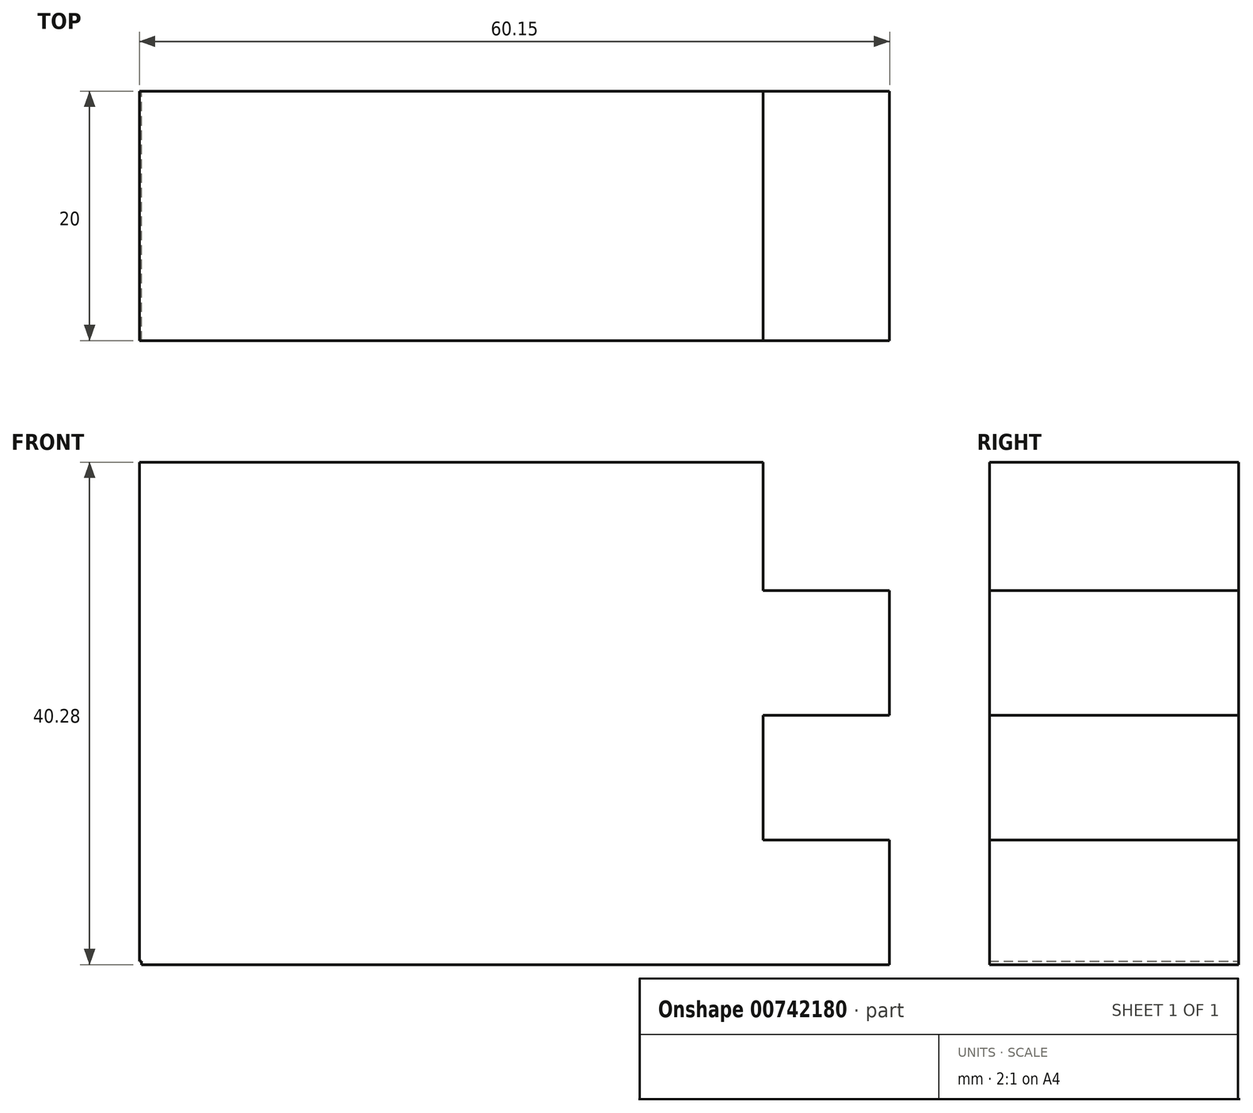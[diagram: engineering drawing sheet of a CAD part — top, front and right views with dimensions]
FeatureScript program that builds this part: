
annotation { "Feature Type Name" : "Feature", "Feature Type Description" : "" }
export const myFeature = defineFeature(function(context is Context, id is Id, definition is map)
    precondition{}
    {
        {
            var Q0;
            Q0=qCreatedBy(makeId("Front.planeOp"),FACE);
            var sketch = newSketch(context, id + "F0", { "sketchPlane" : qUnion([Q0])});
            skLineSegment(sketch, "E0.bottom", {"start": v(-3.97, 22.58) * mm, "end": v(46.03, 22.58) * mm});
            skLineSegment(sketch, "E0.top", {"start": v(-3.97, -17.42) * mm, "end": v(46.03, -17.42) * mm});
            skLineSegment(sketch, "E0.left", {"start": v(-3.97, 22.58) * mm, "end": v(-3.97, -17.42) * mm});
            skLineSegment(sketch, "E0.right", {"start": v(46.03, 22.58) * mm, "end": v(46.03, -17.42) * mm});
            skSolve(sketch);
        }
        {
            var Q0;
            Q0=qCreatedBy(makeId("Front.planeOp"),FACE);
            var sketch = newSketch(context, id + "F1", { "sketchPlane" : qUnion([Q0])});
            skLineSegment(sketch, "E1.bottom", {"start": v(-3.82, -7.7) * mm, "end": v(56.18, -7.7) * mm});
            skLineSegment(sketch, "E1.top", {"start": v(-3.82, -17.7) * mm, "end": v(56.18, -17.7) * mm});
            skLineSegment(sketch, "E1.left", {"start": v(-3.82, -7.7) * mm, "end": v(-3.82, -17.7) * mm});
            skLineSegment(sketch, "E1.right", {"start": v(56.18, -7.7) * mm, "end": v(56.18, -17.7) * mm});
            skLineSegment(sketch, "E2", {"start": v(36.18, -7.7) * mm, "end": v(36.18, 12.3) * mm});
            skLineSegment(sketch, "E3", {"start": v(56.18, -7.7) * mm, "end": v(56.18, 12.3) * mm});
            skLineSegment(sketch, "E4", {"start": v(36.18, 12.3) * mm, "end": v(56.18, 12.3) * mm});
            skLineSegment(sketch, "E5.top", {"start": v(36.18, 2.3) * mm, "end": v(56.18, 2.3) * mm});
            skLineSegment(sketch, "E5.left", {"start": v(36.18, 12.3) * mm, "end": v(36.18, 2.3) * mm});
            skLineSegment(sketch, "E5.right", {"start": v(56.18, 12.3) * mm, "end": v(56.18, 2.3) * mm});
            skSolve(sketch);
        }
        {
            var Q0;
            Q0 = qSketchRegion(id + "F0", true);
            extrude(context, id + "F2", {"entities" : qUnion([Q0]), "depth" : 20 * mm, "offsetDistance" : 25 * mm});
        }
        {
            var Q0;
            Q0=makeQuery(id+"F1.imprint","IMPRINT",FACE,{"disambiguationData":[TD([[makeQuery(id+"F1.imprint","IMPRINT",EDGE,{"derivedFrom":sQuery(id+"F1.wireOp",EDGE,"E4")}),-1.0]])]});
            extrude(context, id + "F3", {"entities" : qUnion([Q0]), "operationType" : NewBodyOperationType.ADD, "depth" : 20 * mm, "offsetDistance" : 25 * mm});
        }
        {
            var Q0;
            Q0=makeQuery(id+"F1.imprint","IMPRINT",FACE,{"disambiguationData":[TD([[makeQuery(id+"F1.imprint","IMPRINT",EDGE,{"derivedFrom":sQuery(id+"F1.wireOp",EDGE,"E1.top")}),1.0]])]});
            extrude(context, id + "F4", {"entities" : qUnion([Q0]), "operationType" : NewBodyOperationType.ADD, "depth" : 20 * mm, "offsetDistance" : 25 * mm});
        }
    });
